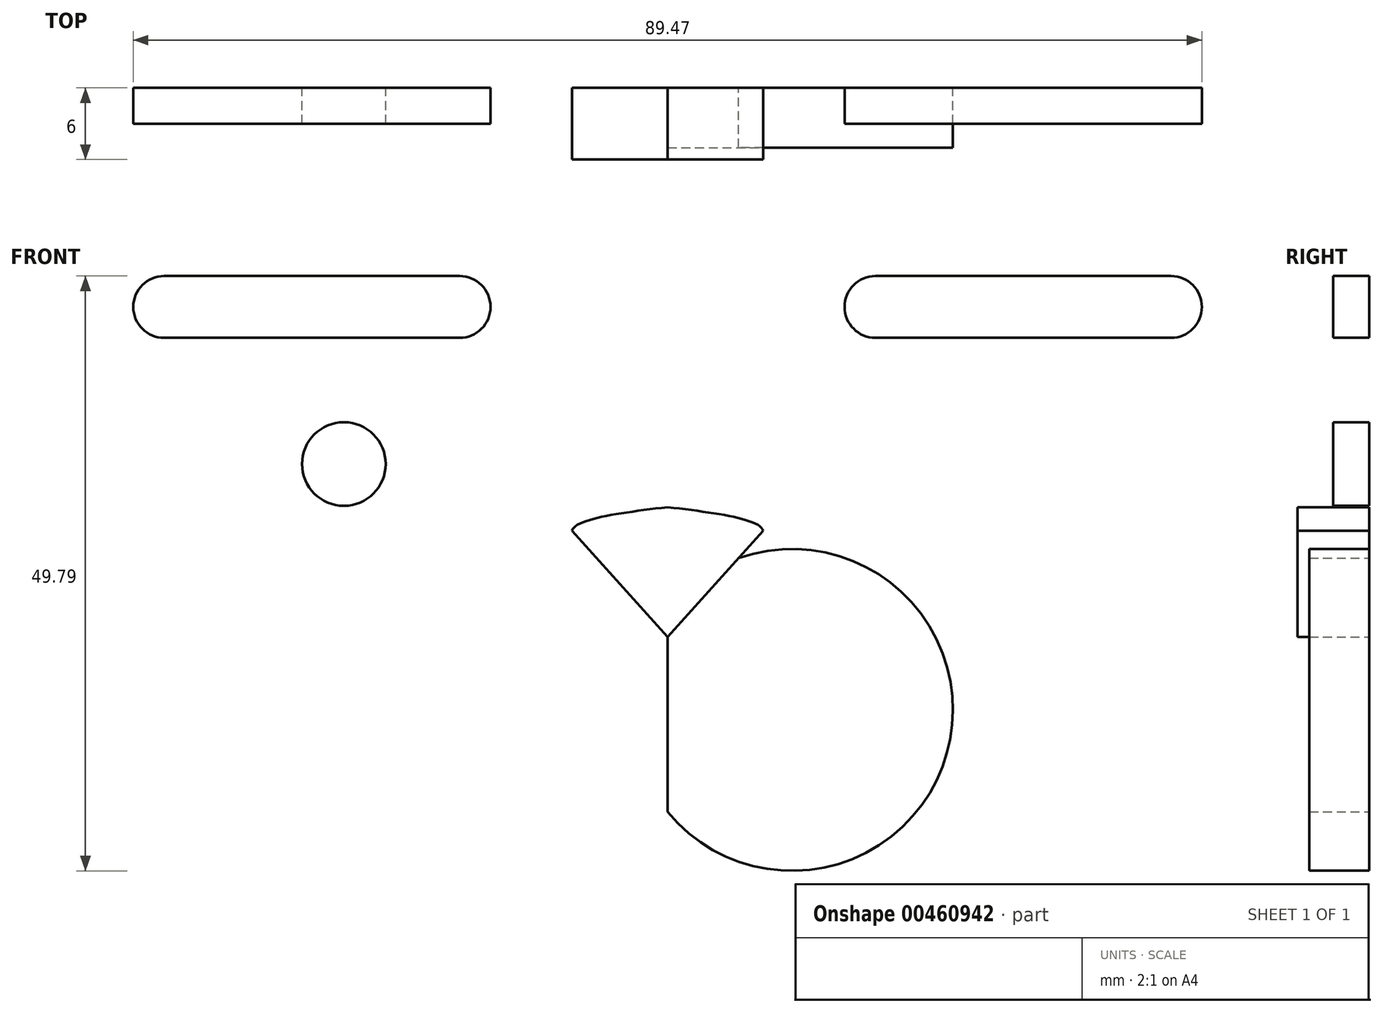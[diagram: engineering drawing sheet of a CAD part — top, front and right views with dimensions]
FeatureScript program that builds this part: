
annotation { "Feature Type Name" : "Feature", "Feature Type Description" : "" }
export const myFeature = defineFeature(function(context is Context, id is Id, definition is map)
    precondition{}
    {
        {
            var Q0;
            Q0=qCreatedBy(makeId("Front.planeOp"),FACE);
            var sketch = newSketch(context, id + "F0", { "sketchPlane" : qUnion([Q0])});
            skLineSegment(sketch, "E0", {"start": v(3.74, -18.18) * mm, "end": v(11.75, -9.3) * mm});
            skLineSegment(sketch, "E1", {"start": v(2.48, -16.79) * mm, "end": v(-4.27, -9.3) * mm});
            skLineSegment(sketch, "E2.bottom", {"start": v(-13.67, 6.85) * mm, "end": v(-38.4, 6.85) * mm});
            skLineSegment(sketch, "E2.top", {"start": v(-13.67, 12.02) * mm, "end": v(-38.4, 12.02) * mm});
            skPoint(sketch, "E2.middle", {"position": v(-26.04, 9.43) * mm});
            skPoint(sketch, "E2.middle.positionSnap0", {"position": v(-21.14, 9.43) * mm});
            skPoint(sketch, "E2.centerSnap0", {"position": v(-21.14, 9.43) * mm});
            skLineSegment(sketch, "E3.MirrorCS", {"start": v(21.15, 12.02) * mm, "end": v(45.89, 12.02) * mm});
            skLineSegment(sketch, "E4.MirrorCS", {"start": v(21.15, 6.85) * mm, "end": v(45.89, 6.85) * mm});
            skArc(sketch, "E5", {"start": v(-38.4, 12.02) * mm, "mid": v(-41, 9.43) * mm, "end": v(-38.4, 6.85) * mm});
            skArc(sketch, "E6", {"start": v(-13.67, 12.02) * mm, "mid": v(-11.08, 9.43) * mm, "end": v(-13.67, 6.85) * mm});
            skArc(sketch, "E7.MirrorCS", {"start": v(45.89, 12.02) * mm, "mid": v(48.47, 9.43) * mm, "end": v(45.89, 6.85) * mm});
            skArc(sketch, "E8.MirrorCS", {"start": v(21.15, 12.02) * mm, "mid": v(18.56, 9.43) * mm, "end": v(21.15, 6.85) * mm});
            skCircle(sketch, "E9", {"center": v(-23.36, -3.71) * mm, "radius": 3.5 * mm});
            skCircle(sketch, "E10.MirrorC", {"center": v(30.84, -3.71) * mm, "radius": 3.5 * mm});
            skArc(sketch, "E11", {"start": v(3.74, -32.84) * mm, "mid": v(-19.64, -27.92) * mm, "end": v(-2.2, -11.6) * mm});
            skArc(sketch, "E12.MirrorCS", {"start": v(3.74, -32.84) * mm, "mid": v(27.12, -27.92) * mm, "end": v(9.68, -11.6) * mm});
            skLineSegment(sketch, "E13", {"start": v(3.74, -18.18) * mm, "end": v(-2.2, -11.6) * mm});
            skLineSegment(sketch, "E14", {"start": v(3.74, -18.18) * mm, "end": v(9.68, -11.6) * mm});
            skLineSegment(sketch, "E15", {"start": v(3.74, -18.18) * mm, "end": v(3.74, -32.84) * mm});
            skPoint(sketch, "E16.orphan", {"position": v(3.74, -15.75) * mm});
            skFitSpline(sketch, "E17", {"points": [v(-2.2, -11.6) * mm, v(-4.27, -9.3) * mm, v(3.74, -7.32) * mm], "startDerivative": vector(-8.94, 6.6) * mm, "endDerivative": vector(18.61, 2.29) * mm});
            skFitSpline(sketch, "E18.MirrorCS", {"points": [v(9.68, -11.6) * mm, v(11.75, -9.3) * mm, v(3.74, -7.32) * mm], "startDerivative": vector(8.94, 6.6) * mm, "endDerivative": vector(-18.61, 2.29) * mm});
            skPoint(sketch, "E19.orphan", {"position": v(21.15, 6.85) * mm});
            skPoint(sketch, "E20.MirrorCS.end.orphan", {"position": v(21.15, 12.02) * mm});
            skPoint(sketch, "E21.MirrorCS.end.orphan", {"position": v(45.89, 12.02) * mm});
            skPoint(sketch, "E22.start.orphan", {"position": v(45.89, 6.85) * mm});
            skLineSegment(sketch, "E23.trimOffspring", {"start": v(3.74, -18.18) * mm, "end": v(3.74, -78.1) * mm});
            skPoint(sketch, "E24.end.orphan", {"position": v(-46.03, 37.05) * mm});
            skSolve(sketch);
        }
        {
            var Q0;
            Q0=makeQuery(id+"F0.imprint","IMPRINT",FACE,{"disambiguationData":[TD([[makeQuery(id+"F0.imprint","IMPRINT",EDGE,{"derivedFrom":sQuery(id+"F0.wireOp",EDGE,"E2.bottom")}),-1.0]])]});
            var Q1;
            Q1=makeQuery(id+"F0.imprint","IMPRINT",FACE,{"disambiguationData":[TD([[makeQuery(id+"F0.imprint","IMPRINT",EDGE,{"derivedFrom":sQuery(id+"F0.wireOp",EDGE,"E3.MirrorCS")}),-1.0]])]});
            var Q2;
            Q2=makeQuery(id+"F0.imprint","IMPRINT",FACE,{"disambiguationData":[TD([[makeQuery(id+"F0.imprint","IMPRINT",EDGE,{"derivedFrom":sQuery(id+"F0.wireOp",EDGE,"E10.MirrorC")}),-1.0]])]});
            var Q3;
            Q3=makeQuery(id+"F0.imprint","IMPRINT",FACE,{"disambiguationData":[TD([[makeQuery(id+"F0.imprint","IMPRINT",EDGE,{"derivedFrom":sQuery(id+"F0.wireOp",EDGE,"E9")}),1.0]])]});
            extrude(context, id + "F1", {"entities" : qUnion([Q0, Q1, Q2, Q3]), "depth" : 3 * mm});
        }
        {
            var Q0;
            {var subQ0=sQuery(id+"F0.wireOp",EDGE,"E11");Q0=makeQuery(id+"F0.imprint","IMPRINT",FACE,{"disambiguationData":[TD([[makeQuery(id+"F0.imprint","IMPRINT",EDGE,{"derivedFrom":subQ0}),-1.0]])]});}
            var Q1;
            {var subQ0=sQuery(id+"F0.wireOp",EDGE,"E12.MirrorCS");Q1=makeQuery(id+"F0.imprint","IMPRINT",FACE,{"disambiguationData":[TD([[makeQuery(id+"F0.imprint","IMPRINT",EDGE,{"derivedFrom":subQ0}),1.0]])]});}
            extrude(context, id + "F2", {"entities" : qUnion([Q0, Q1]), "depth" : 5 * mm});
        }
        {
            var Q0;
            {var subQ5=sQuery(id+"F0.wireOp",EDGE,"E0");Q0=makeQuery(id+"F0.imprint","IMPRINT",FACE,{"disambiguationData":[TD([[makeQuery(id+"F0.imprint","IMPRINT",EDGE,{"derivedFrom":subQ5}),1.0]])]});}
            extrude(context, id + "F3", {"entities" : qUnion([Q0]), "depth" : 6 * mm});
        }
    });
